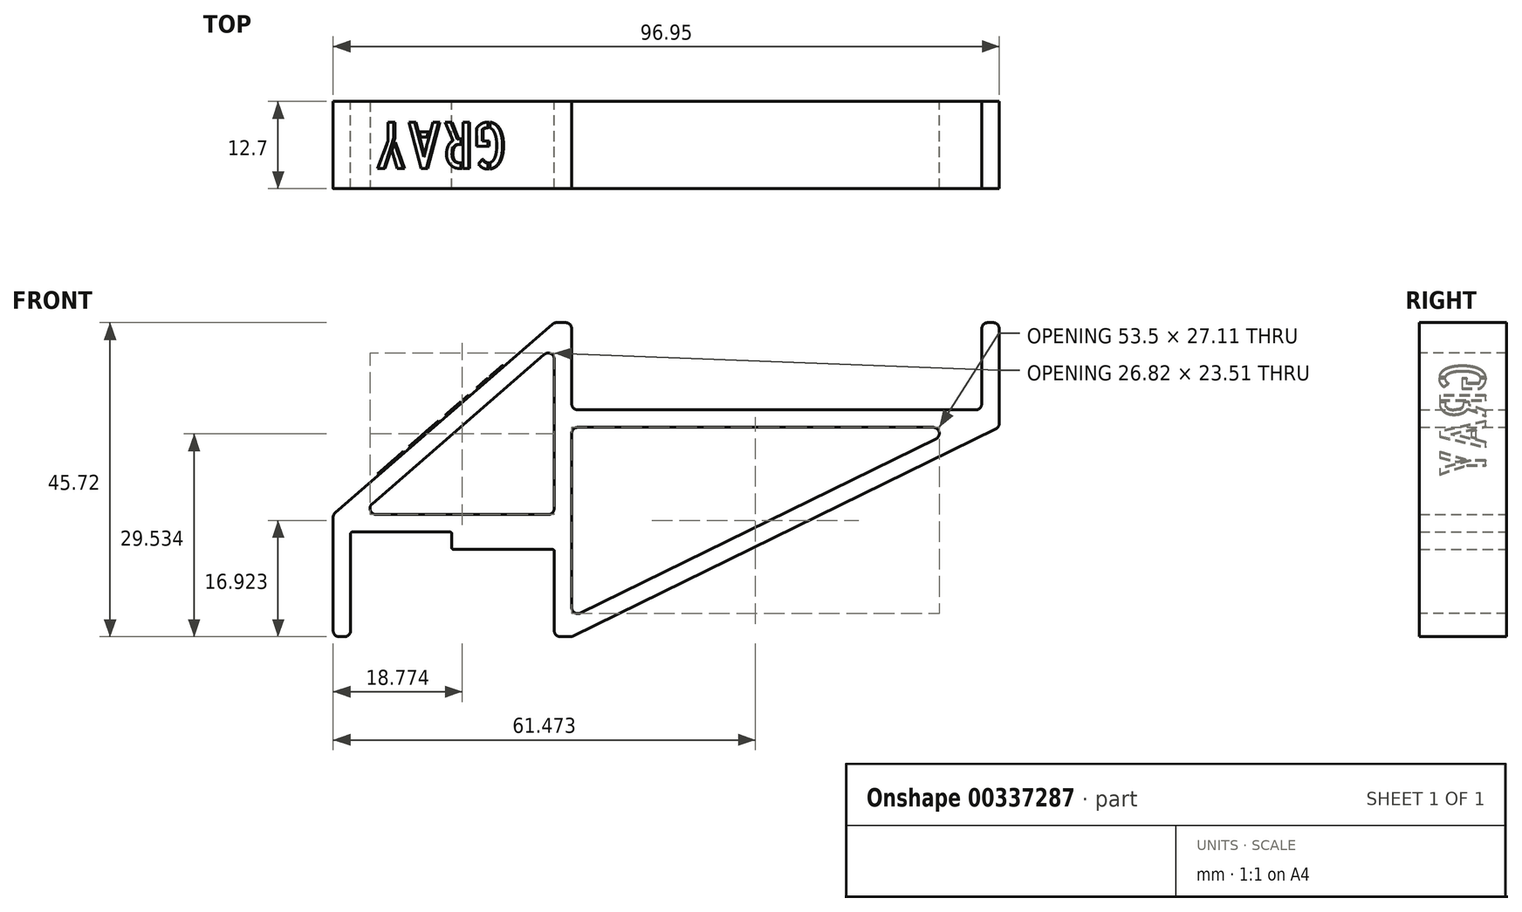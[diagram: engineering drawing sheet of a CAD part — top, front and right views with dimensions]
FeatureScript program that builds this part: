
annotation { "Feature Type Name" : "Feature", "Feature Type Description" : "" }
export const myFeature = defineFeature(function(context is Context, id is Id, definition is map)
    precondition{}
    {
        {
            var Q0;
            Q0=qCreatedBy(makeId("Front.planeOp"),FACE);
            var sketch = newSketch(context, id + "F0", { "sketchPlane" : qUnion([Q0])});
            skLineSegment(sketch, "E0", {"start": v(2.54, 17.78) * mm, "end": v(2.54, 15.24) * mm});
            skLineSegment(sketch, "E1", {"start": v(2.54, 15.24) * mm, "end": v(32.18, 15.24) * mm});
            skLineSegment(sketch, "E2", {"start": v(17.27, 15.24) * mm, "end": v(17.27, 12.7) * mm});
            skLineSegment(sketch, "E3", {"start": v(2.54, 17.78) * mm, "end": v(32.18, 17.78) * mm});
            skLineSegment(sketch, "E4", {"start": v(17.27, 12.7) * mm, "end": v(32.18, 12.7) * mm});
            skLineSegment(sketch, "E5", {"start": v(32.18, 12.7) * mm, "end": v(32.18, 17.78) * mm});
            skLineSegment(sketch, "E6", {"start": v(32.18, 17.78) * mm, "end": v(34.72, 17.78) * mm});
            skLineSegment(sketch, "E7", {"start": v(34.72, 17.78) * mm, "end": v(34.72, 0) * mm});
            skLineSegment(sketch, "E8", {"start": v(32.18, 12.7) * mm, "end": v(32.18, 0) * mm});
            skLineSegment(sketch, "E9", {"start": v(2.54, 17.78) * mm, "end": v(0, 17.78) * mm});
            skLineSegment(sketch, "E10", {"start": v(2.54, 15.24) * mm, "end": v(2.54, 0) * mm});
            skLineSegment(sketch, "E11", {"start": v(0, 17.78) * mm, "end": v(0, 0) * mm});
            skLineSegment(sketch, "E12", {"start": v(0, 0) * mm, "end": v(2.54, 0) * mm});
            skLineSegment(sketch, "E13", {"start": v(34.72, 17.78) * mm, "end": v(34.72, 13.97) * mm});
            skLineSegment(sketch, "E14", {"start": v(32.18, 0) * mm, "end": v(34.72, 0) * mm});
            skLineSegment(sketch, "E15", {"start": v(32.18, 17.78) * mm, "end": v(32.18, 20.32) * mm});
            skLineSegment(sketch, "E16", {"start": v(32.18, 20.32) * mm, "end": v(32.18, 33.02) * mm});
            skLineSegment(sketch, "E17", {"start": v(32.18, 33.02) * mm, "end": v(34.72, 33.02) * mm});
            skLineSegment(sketch, "E18", {"start": v(34.72, 33.02) * mm, "end": v(34.72, 17.78) * mm});
            skLineSegment(sketch, "E19", {"start": v(34.72, 33.02) * mm, "end": v(96.95, 33.02) * mm});
            skLineSegment(sketch, "E20", {"start": v(96.95, 33.02) * mm, "end": v(96.95, 30.48) * mm});
            skLineSegment(sketch, "E21", {"start": v(34.72, 30.48) * mm, "end": v(96.95, 30.48) * mm});
            skLineSegment(sketch, "E22", {"start": v(32.18, 33.02) * mm, "end": v(32.18, 45.72) * mm});
            skLineSegment(sketch, "E23", {"start": v(32.18, 45.72) * mm, "end": v(34.72, 45.72) * mm});
            skLineSegment(sketch, "E24", {"start": v(34.72, 33.02) * mm, "end": v(34.72, 45.72) * mm});
            skLineSegment(sketch, "E25", {"start": v(96.95, 33.02) * mm, "end": v(96.95, 45.72) * mm});
            skLineSegment(sketch, "E26", {"start": v(96.95, 45.72) * mm, "end": v(94.41, 45.72) * mm});
            skLineSegment(sketch, "E27", {"start": v(94.41, 45.72) * mm, "end": v(94.41, 33.02) * mm});
            skLineSegment(sketch, "E28", {"start": v(34.72, 0) * mm, "end": v(96.95, 30.48) * mm});
            skLineSegment(sketch, "E29", {"start": v(34.72, 2.83) * mm, "end": v(91.18, 30.48) * mm});
            skLineSegment(sketch, "E30", {"start": v(0, 17.78) * mm, "end": v(32.18, 45.72) * mm});
            skLineSegment(sketch, "E31", {"start": v(32.18, 42.36) * mm, "end": v(3.87, 17.78) * mm});
            skSolve(sketch);
        }
        {
            var Q0;
            {var subQ0=sQuery(id+"F0.wireOp",EDGE,"jvLbMz3n-FQXq-gv2P-DcQT-8QfjgkFX3igj");Q0=makeQuery(id+"F0.imprint","IMPRINT",FACE,{"disambiguationData":[TD([[makeQuery(id+"F0.imprint","IMPRINT",EDGE,{"derivedFrom":subQ0}),1.0]])]});}
            var Q1;
            {var subQ4=sQuery(id+"F0.wireOp",EDGE,"E6");Q1=makeQuery(id+"F0.imprint","IMPRINT",FACE,{"disambiguationData":[TD([[makeQuery(id+"F0.imprint","IMPRINT",EDGE,{"derivedFrom":subQ4}),1.0]])]});}
            var Q2;
            {var subQ0=sQuery(id+"F0.wireOp",EDGE,"5fyH0i7X-IWu1-a1HD-RHR6-HmbiZMtqhNbi");Q2=makeQuery(id+"F0.imprint","IMPRINT",FACE,{"disambiguationData":[TD([[makeQuery(id+"F0.imprint","IMPRINT",EDGE,{"derivedFrom":subQ0}),-1.0]])]});}
            var Q3;
            {var subQ3=sQuery(id+"F0.wireOp",EDGE,"E6");Q3=makeQuery(id+"F0.imprint","IMPRINT",FACE,{"disambiguationData":[TD([[makeQuery(id+"F0.imprint","IMPRINT",EDGE,{"derivedFrom":subQ3}),-1.0]])]});}
            var Q4;
            {var subQ0=sQuery(id+"F0.wireOp",EDGE,"E17");Q4=makeQuery(id+"F0.imprint","IMPRINT",FACE,{"disambiguationData":[TD([[makeQuery(id+"F0.imprint","IMPRINT",EDGE,{"derivedFrom":subQ0}),-1.0]])]});}
            var Q5;
            {var subQ1=sQuery(id+"F0.wireOp",EDGE,"E9");Q5=makeQuery(id+"F0.imprint","IMPRINT",FACE,{"disambiguationData":[TD([[makeQuery(id+"F0.imprint","IMPRINT",EDGE,{"derivedFrom":subQ1}),-1.0]])]});}
            var Q6;
            {var subQ1=sQuery(id+"F0.wireOp",EDGE,"E0");Q6=makeQuery(id+"F0.imprint","IMPRINT",FACE,{"disambiguationData":[TD([[makeQuery(id+"F0.imprint","IMPRINT",EDGE,{"derivedFrom":subQ1}),1.0]])]});}
            var Q7;
            {var subQ3=sQuery(id+"F0.wireOp",EDGE,"E2");Q7=makeQuery(id+"F0.imprint","IMPRINT",FACE,{"disambiguationData":[TD([[makeQuery(id+"F0.imprint","IMPRINT",EDGE,{"derivedFrom":subQ3}),1.0]])]});}
            var Q8;
            Q8=makeQuery(id+"F0.imprint","IMPRINT",FACE,{"disambiguationData":[TD([[makeQuery(id+"F0.imprint","IMPRINT",EDGE,{"derivedFrom":sQuery(id+"F0.wireOp",EDGE,"E0")}),-1.0]])]});
            var Q9;
            {var subQ0=sQuery(id+"F0.wireOp",EDGE,"E28");Q9=makeQuery(id+"F0.imprint","IMPRINT",FACE,{"disambiguationData":[TD([[makeQuery(id+"F0.imprint","IMPRINT",EDGE,{"derivedFrom":subQ0}),1.0]])]});}
            var Q10;
            {var subQ0=sQuery(id+"F0.wireOp",EDGE,"E20");Q10=makeQuery(id+"F0.imprint","IMPRINT",FACE,{"disambiguationData":[TD([[makeQuery(id+"F0.imprint","IMPRINT",EDGE,{"derivedFrom":subQ0}),-1.0]])]});}
            var Q11;
            {var subQ0=sQuery(id+"F0.wireOp",EDGE,"E25");Q11=makeQuery(id+"F0.imprint","IMPRINT",FACE,{"disambiguationData":[TD([[makeQuery(id+"F0.imprint","IMPRINT",EDGE,{"derivedFrom":subQ0}),1.0]])]});}
            var Q12;
            Q12=makeQuery(id+"F0.imprint","IMPRINT",FACE,{"disambiguationData":[TD([[makeQuery(id+"F0.imprint","IMPRINT",EDGE,{"derivedFrom":sQuery(id+"F0.wireOp",EDGE,"E17")}),1.0]])]});
            extrude(context, id + "F1", {"entities" : qUnion([Q0, Q1, Q2, Q3, Q4, Q5, Q6, Q7, Q8, Q9, Q10, Q11, Q12]), "depth" : 12.7 * mm, "offsetDistance" : 25.4 * mm});
        }
        {
            var Q0;
            Q0=makeQuery(id+"F1.opExtrude","SWEPT_EDGE",EDGE,{"disambiguationData":[OSD([sQuery(id+"F0.wireOp",EDGE,"E11"),sQuery(id+"F0.wireOp",EDGE,"E12")])]});
            var Q1;
            Q1=makeQuery(id+"F1.opExtrude","SWEPT_EDGE",EDGE,{"disambiguationData":[OSD([sQuery(id+"F0.wireOp",EDGE,"E10"),sQuery(id+"F0.wireOp",EDGE,"E12")])]});
            var Q2;
            Q2=makeQuery(id+"F1.opExtrude","SWEPT_EDGE",EDGE,{"disambiguationData":[OSD([sQuery(id+"F0.wireOp",EDGE,"E8"),sQuery(id+"F0.wireOp",EDGE,"E14")])]});
            var Q3;
            Q3=makeQuery(id+"F1.opExtrude","SWEPT_EDGE",EDGE,{"disambiguationData":[OSD([sQuery(id+"F0.wireOp",EDGE,"E7"),sQuery(id+"F0.wireOp",EDGE,"E14"),sQuery(id+"F0.wireOp",EDGE,"5fyH0i7X-IWu1-a1HD-RHR6-HmbiZMtqhNbi")])]});
            var Q4;
            Q4=makeQuery(id+"F1.opExtrude","SWEPT_EDGE",EDGE,{"disambiguationData":[OSD([sQuery(id+"F0.wireOp",EDGE,"XK4gZvIV-EjMV-5yAQ-Ko4O-cfLP38Z1F7WN"),sQuery(id+"F0.wireOp",EDGE,"7Lkjueb4-pT6m-45AM-mPG1-UAD8002npaEU"),sQuery(id+"F0.wireOp",EDGE,"5fyH0i7X-IWu1-a1HD-RHR6-HmbiZMtqhNbi")])]});
            var Q5;
            Q5=makeQuery(id+"F1.opExtrude","SWEPT_EDGE",EDGE,{"disambiguationData":[OSD([sQuery(id+"F0.wireOp",EDGE,"jvLbMz3n-FQXq-gv2P-DcQT-8QfjgkFX3igj"),sQuery(id+"F0.wireOp",EDGE,"qnbmaB5V-popD-AF3a-DfRj-HsTCZiOA8s9y")])]});
            var Q6;
            Q6=makeQuery(id+"F1.opExtrude","SWEPT_EDGE",EDGE,{"disambiguationData":[OSD([sQuery(id+"F0.wireOp",EDGE,"qnbmaB5V-popD-AF3a-DfRj-HsTCZiOA8s9y"),sQuery(id+"F0.wireOp",EDGE,"aIP8VWIh-LyoE-sRiJ-CMpf-Z2WFARpvebgj")])]});
            var Q7;
            Q7=makeQuery(id+"F1.opExtrude","SWEPT_EDGE",EDGE,{"disambiguationData":[OSD([sQuery(id+"F0.wireOp",EDGE,"6lxfTYoy-XcvB-1Uv5-WnG9-A3RQKU2m3VZt"),sQuery(id+"F0.wireOp",EDGE,"aIP8VWIh-LyoE-sRiJ-CMpf-Z2WFARpvebgj")])]});
            var Q8;
            Q8=makeQuery(id+"F1.opExtrude","SWEPT_EDGE",EDGE,{"disambiguationData":[OSD([sQuery(id+"F0.wireOp",EDGE,"6lxfTYoy-XcvB-1Uv5-WnG9-A3RQKU2m3VZt"),sQuery(id+"F0.wireOp",EDGE,"DMFJkJL7-YD1f-RirW-OZ3E-zvg2S2j0YXvj")])]});
            var Q9;
            Q9=makeQuery(id+"F1.opExtrude","SWEPT_EDGE",EDGE,{"disambiguationData":[OSD([sQuery(id+"F0.wireOp",EDGE,"E17"),sQuery(id+"F0.wireOp",EDGE,"DMFJkJL7-YD1f-RirW-OZ3E-zvg2S2j0YXvj")])]});
            var Q10;
            Q10=makeQuery(id+"F1.opExtrude","SWEPT_EDGE",EDGE,{"disambiguationData":[OSD([sQuery(id+"F0.wireOp",EDGE,"E16"),sQuery(id+"F0.wireOp",EDGE,"E17"),sQuery(id+"F0.wireOp",EDGE,"AtPNPN8x-o45G-cI4L-aAtb-2XYuBCvoHzdQ")])]});
            var Q11;
            Q11=makeQuery(id+"F1.opExtrude","SWEPT_EDGE",EDGE,{"disambiguationData":[OSD([sQuery(id+"F0.wireOp",EDGE,"E9"),sQuery(id+"F0.wireOp",EDGE,"E11"),sQuery(id+"F0.wireOp",EDGE,"AtPNPN8x-o45G-cI4L-aAtb-2XYuBCvoHzdQ")])]});
            var Q12;
            Q12=makeQuery(id+"F1.opExtrude","SWEPT_EDGE",EDGE,{"disambiguationData":[OSD([sQuery(id+"F0.wireOp",EDGE,"E3"),sQuery(id+"F0.wireOp",EDGE,"E5"),sQuery(id+"F0.wireOp",EDGE,"E6"),sQuery(id+"F0.wireOp",EDGE,"E15")])]});
            var Q13;
            Q13=makeQuery(id+"F1.opExtrude","SWEPT_EDGE",EDGE,{"disambiguationData":[OSD([sQuery(id+"F0.wireOp",EDGE,"E16"),sQuery(id+"F0.wireOp",EDGE,"zp0DIl8D-M6z1-Rd7q-iDpY-U8eUNXUtOqLU")])]});
            var Q14;
            Q14=makeQuery(id+"F1.opExtrude","SWEPT_EDGE",EDGE,{"disambiguationData":[OSD([sQuery(id+"F0.wireOp",EDGE,"E3"),sQuery(id+"F0.wireOp",EDGE,"zp0DIl8D-M6z1-Rd7q-iDpY-U8eUNXUtOqLU")])]});
            var Q15;
            Q15=makeQuery(id+"F1.opExtrude","SWEPT_EDGE",EDGE,{"disambiguationData":[OSD([sQuery(id+"F0.wireOp",EDGE,"E6"),sQuery(id+"F0.wireOp",EDGE,"E13"),sQuery(id+"F0.wireOp",EDGE,"XK4gZvIV-EjMV-5yAQ-Ko4O-cfLP38Z1F7WN")])]});
            var Q16;
            Q16=makeQuery(id+"F1.opExtrude","SWEPT_EDGE",EDGE,{"disambiguationData":[OSD([sQuery(id+"F0.wireOp",EDGE,"XK4gZvIV-EjMV-5yAQ-Ko4O-cfLP38Z1F7WN"),sQuery(id+"F0.wireOp",EDGE,"Zk52e19d-0mzT-GTo3-gYqh-DDcSyQSH87MV")])]});
            var Q17;
            Q17=makeQuery(id+"F1.opExtrude","SWEPT_EDGE",EDGE,{"disambiguationData":[OSD([sQuery(id+"F0.wireOp",EDGE,"E7"),sQuery(id+"F0.wireOp",EDGE,"Zk52e19d-0mzT-GTo3-gYqh-DDcSyQSH87MV")])]});
            var Q18;
            Q18=makeQuery(id+"F1.opExtrude","SWEPT_EDGE",EDGE,{"disambiguationData":[OSD([sQuery(id+"F0.wireOp",EDGE,"E18"),sQuery(id+"F0.wireOp",EDGE,"E21")])]});
            var Q19;
            Q19=makeQuery(id+"F1.opExtrude","SWEPT_EDGE",EDGE,{"disambiguationData":[OSD([sQuery(id+"F0.wireOp",EDGE,"E21"),sQuery(id+"F0.wireOp",EDGE,"E29")])]});
            var Q20;
            Q20=makeQuery(id+"F1.opExtrude","SWEPT_EDGE",EDGE,{"disambiguationData":[OSD([sQuery(id+"F0.wireOp",EDGE,"E20"),sQuery(id+"F0.wireOp",EDGE,"E21"),sQuery(id+"F0.wireOp",EDGE,"E28")])]});
            var Q21;
            Q21=makeQuery(id+"F1.opExtrude","SWEPT_EDGE",EDGE,{"disambiguationData":[OSD([sQuery(id+"F0.wireOp",EDGE,"E25"),sQuery(id+"F0.wireOp",EDGE,"E26")])]});
            var Q22;
            Q22=makeQuery(id+"F1.opExtrude","SWEPT_EDGE",EDGE,{"disambiguationData":[OSD([sQuery(id+"F0.wireOp",EDGE,"E26"),sQuery(id+"F0.wireOp",EDGE,"E27")])]});
            var Q23;
            Q23=makeQuery(id+"F1.opExtrude","SWEPT_EDGE",EDGE,{"disambiguationData":[OSD([sQuery(id+"F0.wireOp",EDGE,"E19"),sQuery(id+"F0.wireOp",EDGE,"E27")])]});
            var Q24;
            Q24=makeQuery(id+"F1.opExtrude","SWEPT_EDGE",EDGE,{"disambiguationData":[OSD([sQuery(id+"F0.wireOp",EDGE,"E22"),sQuery(id+"F0.wireOp",EDGE,"E23")])]});
            var Q25;
            Q25=makeQuery(id+"F1.opExtrude","SWEPT_EDGE",EDGE,{"disambiguationData":[OSD([sQuery(id+"F0.wireOp",EDGE,"E23"),sQuery(id+"F0.wireOp",EDGE,"E24")])]});
            var Q26;
            Q26=makeQuery(id+"F1.opExtrude","SWEPT_EDGE",EDGE,{"disambiguationData":[OSD([sQuery(id+"F0.wireOp",EDGE,"E22"),sQuery(id+"F0.wireOp",EDGE,"E31")])]});
            fillet(context, id + "F2", {"entities" : qUnion([Q0, Q1, Q2, Q3, Q4, Q5, Q6, Q7, Q8, Q9, Q10, Q11, Q12, Q13, Q14, Q15, Q16, Q17, Q18, Q19, Q20, Q21, Q22, Q23, Q24, Q25, Q26]), "tangentPropagation" : true, "radius" : 0.89 * mm, "defaultsChanged" : false, "vertexSettings" : [], "allowEdgeOverflow" : false});
        }
        {
            var Q0;
            Q0=makeQuery(id+"F1.opExtrude","SWEPT_EDGE",EDGE,{"disambiguationData":[OSD([sQuery(id+"F0.wireOp",EDGE,"E0"),sQuery(id+"F0.wireOp",EDGE,"E1"),sQuery(id+"F0.wireOp",EDGE,"E10")])]});
            var Q1;
            Q1=makeQuery(id+"F1.opExtrude","SWEPT_EDGE",EDGE,{"disambiguationData":[OSD([sQuery(id+"F0.wireOp",EDGE,"E1"),sQuery(id+"F0.wireOp",EDGE,"E2")])]});
            var Q2;
            Q2=makeQuery(id+"F1.opExtrude","SWEPT_EDGE",EDGE,{"disambiguationData":[OSD([sQuery(id+"F0.wireOp",EDGE,"E2"),sQuery(id+"F0.wireOp",EDGE,"E4")])]});
            var Q3;
            Q3=makeQuery(id+"F1.opExtrude","SWEPT_EDGE",EDGE,{"disambiguationData":[OSD([sQuery(id+"F0.wireOp",EDGE,"E4"),sQuery(id+"F0.wireOp",EDGE,"E5"),sQuery(id+"F0.wireOp",EDGE,"E8")])]});
            fillet(context, id + "F3", {"entities" : qUnion([Q0, Q1, Q2, Q3]), "tangentPropagation" : true, "radius" : 0.25 * mm, "defaultsChanged" : true, "vertexSettings" : [], "allowEdgeOverflow" : false});
        }
        {
            var Q0;
            Q0=makeQuery(id+"F1.opExtrude","SWEPT_FACE",FACE,{"disambiguationData":[OSD([sQuery(id+"F0.wireOp",EDGE,"E30")])]});
            var sketch = newSketch(context, id + "F4", { "sketchPlane" : qUnion([Q0])});
            skText(sketch, "E32", { "text": "GRAY", "fontName": "AllertaStencil-Regular.ttf"});
            const initialGuessF4  = {"E32": [0.04523, -0.00306, -1, 0, 0.00669]};
            skSetInitialGuess(sketch, initialGuessF4);
            skSolve(sketch);
        }
        {
            var Q0;
            Q0 = qSketchRegion(id + "F4", true);
            extrude(context, id + "F5", {"entities" : qUnion([Q0]), "operationType" : NewBodyOperationType.ADD, "depth" : 0.25 * mm, "offsetDistance" : 25.4 * mm});
        }
    });
